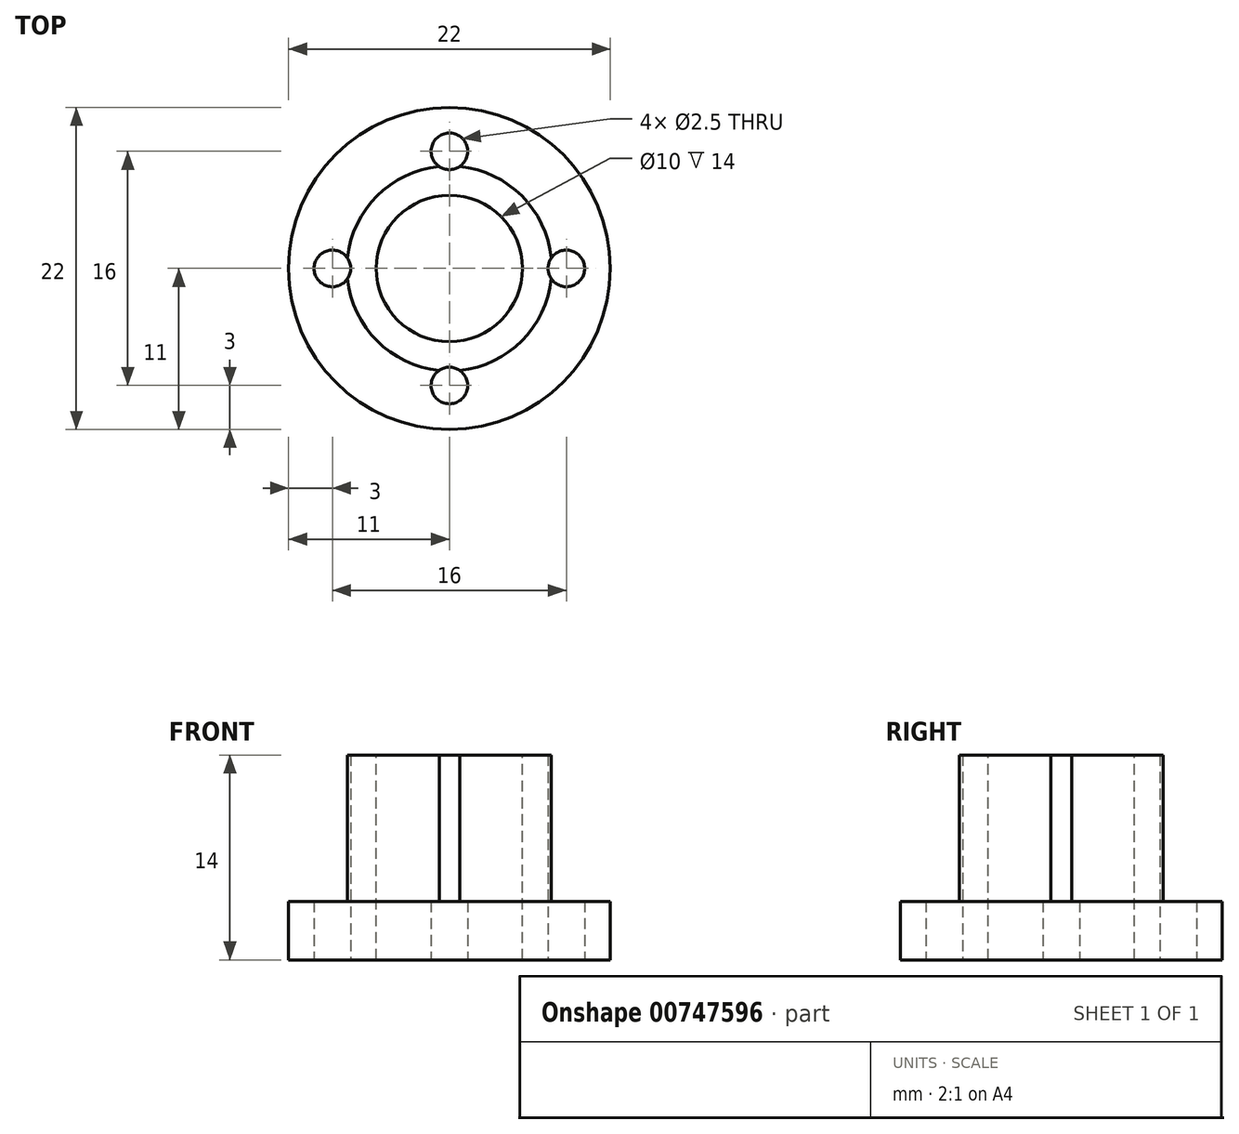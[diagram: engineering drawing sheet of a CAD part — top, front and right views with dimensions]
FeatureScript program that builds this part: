
annotation { "Feature Type Name" : "Feature", "Feature Type Description" : "" }
export const myFeature = defineFeature(function(context is Context, id is Id, definition is map)
    precondition{}
    {
        {
            var Q0;
            Q0=qCreatedBy(makeId("Front.planeOp"),FACE);
            var sketch = newSketch(context, id + "F0", { "sketchPlane" : qUnion([Q0])});
            skLineSegment(sketch, "E0", {"start": v(0, 30.4) * mm, "end": v(0, -33.6) * mm, "construction": true});
            skLineSegment(sketch, "E1.0", {"start": v(-5, 14) * mm, "end": v(-5, 0) * mm});
            skLineSegment(sketch, "E2.0", {"start": v(-11, 4) * mm, "end": v(-11, 0) * mm});
            skLineSegment(sketch, "E3", {"start": v(0, 0) * mm, "end": v(-11, 0) * mm});
            skLineSegment(sketch, "E4", {"start": v(-11, 0) * mm, "end": v(-11, 4) * mm});
            skLineSegment(sketch, "E5", {"start": v(-11, 4) * mm, "end": v(-7, 4) * mm});
            skLineSegment(sketch, "E6", {"start": v(-7, 4) * mm, "end": v(-7, 14) * mm});
            skLineSegment(sketch, "E7", {"start": v(-7, 14) * mm, "end": v(-5, 14) * mm});
            skSolve(sketch);
        }
        {
            var Q0;
            {var subQ2=sQuery(id+"F0.wireOp",EDGE,"E1.0");Q0=makeQuery(id+"F0.imprint","IMPRINT",FACE,{"disambiguationData":[TD([[makeQuery(id+"F0.imprint","IMPRINT",EDGE,{"derivedFrom":subQ2}),-1.0]])]});}
            var Q1;
            Q1=sQuery(id+"F0.wireOp",EDGE,"E0");
            revolve(context, id + "F1", {"surfaceOperationType" : NewSurfaceOperationType.NEW, "entities" : qUnion([Q0]), "axis" : qUnion([Q1]), "revolveType" : RevolveType.FULL});
        }
        {
            var Q0;
            Q0=makeQuery(id+"F1.opRevolve","SWEPT_FACE",FACE,{"disambiguationData":[OSD([sQuery(id+"F0.wireOp",EDGE,"E3")])]});
            var sketch = newSketch(context, id + "F2", { "sketchPlane" : qUnion([Q0])});
            skCircle(sketch, "E8", {"center": v(0, 8) * mm, "radius": 1.25 * mm});
            skCircle(sketch, "E9", {"center": v(8, 0) * mm, "radius": 1.25 * mm});
            skCircle(sketch, "E10", {"center": v(0, -8) * mm, "radius": 1.25 * mm});
            skCircle(sketch, "E11", {"center": v(-8, 0) * mm, "radius": 1.25 * mm});
            skSolve(sketch);
        }
        {
            var Q0;
            Q0=makeQuery(id+"F2.imprint","IMPRINT",FACE,{"disambiguationData":[TD([[makeQuery(id+"F2.imprint","IMPRINT",EDGE,{"derivedFrom":sQuery(id+"F2.wireOp",EDGE,"E8")}),1.0]])]});
            var Q1;
            Q1=makeQuery(id+"F2.imprint","IMPRINT",FACE,{"disambiguationData":[TD([[makeQuery(id+"F2.imprint","IMPRINT",EDGE,{"derivedFrom":sQuery(id+"F2.wireOp",EDGE,"E11")}),1.0]])]});
            var Q2;
            Q2=makeQuery(id+"F2.imprint","IMPRINT",FACE,{"disambiguationData":[TD([[makeQuery(id+"F2.imprint","IMPRINT",EDGE,{"derivedFrom":sQuery(id+"F2.wireOp",EDGE,"E9")}),1.0]])]});
            var Q3;
            Q3=makeQuery(id+"F2.imprint","IMPRINT",FACE,{"disambiguationData":[TD([[makeQuery(id+"F2.imprint","IMPRINT",EDGE,{"derivedFrom":sQuery(id+"F2.wireOp",EDGE,"E10")}),1.0]])]});
            extrude(context, id + "F3", {"entities" : qUnion([Q0, Q1, Q2, Q3]), "operationType" : NewBodyOperationType.REMOVE, "oppositeDirection" : true, "depth" : 14 * mm, "offsetDistance" : 25 * mm});
        }
    });
